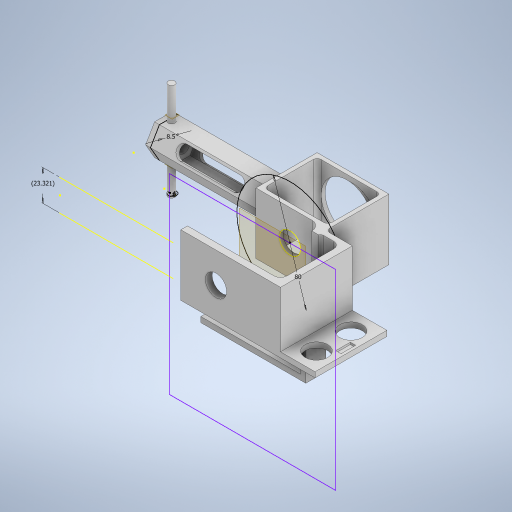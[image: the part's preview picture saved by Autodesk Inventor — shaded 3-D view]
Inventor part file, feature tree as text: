
AUTODESK INVENTOR PART (.ipt)
format: ipt  version: 2024 (Build 280153000, 153)  size: 843,264 bytes
history: native  units: in
note: dims shown in document units (in); Inventor stores cm internally (conversion verified against a paired STEP export)
features: sketch x53, extrude x47, fillet x12, plane x3
ambient origin geometry x8: Origin, YZ Plane, XZ Plane, XY Plane, X Axis, Y Axis, Z Axis, Center Point
bodies: Solid1 (feature_tree)
feature tree (115):
  extrude  "Extrusion1"  Depth=0.0984in
  extrude  "Extrusion2"  Depth=0.3937in TaperAngle=0.0deg
  extrude  "Extrusion3"  Depth=0.3937in TaperAngle=0.0deg
  extrude  "Extrusion4"  Depth=0.1969in
  fillet  "Fillet1"  Radius=2.7559in
  fillet  "Fillet2"  Radius=0.1969in
  extrude  "Extrusion5"  Depth=0.0984in
  extrude  "Extrusion6"  Depth=1.811in
  extrude  "Extrusion7"  Depth=1.811in TaperAngle=0.0deg
  extrude  "Extrusion8"  Depth=0.1181in
  extrude  "Extrusion9"  Depth=0.1181in TaperAngle=0.0deg
  fillet  "Fillet3"  Radius=0.6693in
  fillet  "Fillet4"  Radius=0.1181in
  plane  "Work Plane1"
  extrude  "Extrusion15"  Depth=0.9843in
  extrude  "Extrusion18"  Depth=0.1181in
  extrude  "Extrusion19"  Depth=0.3937in
  extrude  "Extrusion20"  Depth=0.2756in
  extrude  "Extrusion21"  Depth=0.1969in TaperAngle=0.0deg
  extrude  "Extrusion26"  Depth=0.1575in
  fillet  "Fillet9"  Radius=0.7874in
  fillet  "Fillet10"  Radius=0.1969in
  fillet  "Fillet11"  Radius=1.9685in
  fillet  "Fillet12"  Radius=0.1969in
  fillet  "Fillet13"  Radius=2.7559in
  fillet  "Fillet15"  Radius=11.811in
  plane  "Work Plane2"
  extrude  "Extrusion27"  Depth=0.1181in
  plane  "Work Plane3"
  extrude  "Extrusion28"  Depth=0.1969in
  extrude  "Extrusion29"  Depth=0.1575in
  extrude  "Extrusion30"  Depth=0.315in
  sketch  "Sketch35"  dims[d121=0.1181in d122=0.0in d123=-0.748in]
  extrude  "Extrusion31"  [1 undecoded]
  extrude  "Extrusion32"  Depth=0.1575in
  extrude  "Extrusion33"  Depth=0.7087in
  extrude  "Extrusion34"  Depth=0.1575in
  extrude  "Extrusion35"  Depth=0.1575in
  extrude  "Extrusion36"  Depth=0.2362in TaperAngle=0.0deg
  extrude  "Extrusion37"  Depth=0.1181in TaperAngle=0.0deg
  extrude  "Extrusion38"  Depth=0.4724in
  extrude  "Extrusion39"  Depth=3.1102in TaperAngle=0.0deg
  extrude  "Extrusion40"  Depth=3.937in TaperAngle=0.0deg
  sketch  "Sketch46"  dims[d152=3.1496in d153=0.0in d154=0.4331in]
  extrude  "Extrusion41"  Depth=0.1181in
  extrude  "Extrusion42"  Depth=0.4331in
  extrude  "Extrusion43"  Depth=0.3937in
  extrude  "Extrusion44"  Depth=0.2362in
  extrude  "Extrusion45"  Depth=0.9843in TaperAngle=0.0deg
  extrude  "Extrusion46"  Depth=0.1969in
  extrude  "Extrusion47"  Depth=0.1181in
  fillet  "Fillet16"  Radius=0.1181in
  fillet  "Fillet17"  Radius=0.1181in
  extrude  "Extrusion48"  Depth=0.1181in TaperAngle=0.0deg
  extrude  "Extrusion49"  Depth=0.1969in TaperAngle=0.0deg
  sketch  "Sketch56"  dims[d182=0.6299in d183=39.3701in d184=0.0in]
  extrude  "Extrusion50"  Depth=0.4331in TaperAngle=0.0deg
  extrude  "Extrusion51"  Depth=39.3701in TaperAngle=0.0deg
  extrude  "Extrusion52"  Depth=0.1181in TaperAngle=0.0deg
  extrude  "Extrusion53"  Depth=0.2756in
  sketch  "Sketch61"  dims[d196=1.0236in d197=0.0in d198=0.5118in]
  extrude  "Extrusion54"  Depth=0.1181in TaperAngle=0.0deg
  extrude  "Extrusion55"  Depth=0.1575in
  sketch  "Sketch65"  dims[d204=0.0591in d205=0.0in]
  extrude  "Extrusion57"  Depth=0.5118in
  extrude  "Extrusion58"  Depth=1.0236in TaperAngle=0.0deg
  extrude  "Extrusion59"  Depth=0.4331in
  sketch  "Sketch69"  dims[d209=1.063in d210=0.0in]
  sketch  "Sketch72"  dims[d211=3.1496in d212=0.1575in d213=2.9528in d214=0.0in d215=0.1575in d216=0.0in d221=0.5906in d222=0.7874in d223=0.0in d224=0.1969in d225=0.1969in d226=3.937in d227=0.0in d228=0.3937in d229=0.5906in d230=0.0in d231=0.8661in d232=0.1378in d233=0.0in d234=0.3346in d37=0.0in d38=0.0in d39=0.0in d74=0.0197in d75=0.0344in d238=0.0197in d239=0.0344in d240=0.0197in d241=0.0344in d242=0.0197in d243=0.0344in]
  sketch  "Sketch1"  dims[d0=0.3937in d1=0.0984in]
  sketch  "Sketch2"  dims[d2=0.3937in d3=0.0in d4=0.0787in d5=0.0in]
  sketch  "Sketch3"  dims[d6=0.3937in d7=0.0787in d8=0.0in]
  sketch  "Sketch4"  dims[d9=0.2362in d10=0.1969in d11=2.7559in d12=0.0in d13=0.1969in]
  sketch  "Sketch5"  dims[d14=0.1575in d15=0.0984in]
  sketch  "Sketch6"  dims[d16=3.1496in d17=0.0in d18=1.811in]
  sketch  "Sketch8"  dims[d19=1.811in d20=2.126in d21=0.0in]
  sketch  "Sketch9"  dims[d22=0.1181in d23=0.1181in]
  sketch  "Sketch10"  dims[d24=0.1181in d25=1.7717in d26=0.0in d27=0.6693in d28=0.1181in d29=0.0in]
  sketch  "Sketch19"  dims[d30=0.9843in d31=0.6299in]
  sketch  "Sketch22"  dims[d32=1.378in d33=0.0in d34=0.1181in]
  sketch  "Sketch23"  dims[d35=0.0787in d36=0.3937in]
  sketch  "Sketch24"  dims[d72=0.3937in d73=0.0in d80=0.2756in]
  sketch  "Sketch25"  dims[d81=1.378in d82=0.1969in d83=0.0in]
  sketch  "Sketch30"  dims[d84=0.1378in d85=0.1575in d86=0.7874in d87=0.0in d88=0.1969in d89=1.9685in d90=0.0in d91=0.1969in d92=2.7559in d93=0.0in d110=11.811in d111=0.0in]
  sketch  "Sketch31"  dims[d112=0.1181in d113=0.1181in]
  sketch  "Sketch32"  dims[d114=0.2677in d115=0.1969in]
  sketch  "Sketch33"  dims[d116=0.1969in d118=0.1575in]
  sketch  "Sketch34"  dims[d119=-0.748in d120=0.315in]
  sketch  "Sketch36"  dims[d124=0.1181in d125=0.0in d126=0.1575in]
  sketch  "Sketch37"  dims[d127=3.937in d128=0.0in d129=0.7087in]
  sketch  "Sketch38"  dims[d130=0.1181in d131=0.0in d132=0.1575in]
  sketch  "Sketch39"  dims[d133=0.2362in d134=0.1575in]
  sketch  "Sketch40"  dims[d135=0.2362in d136=0.6299in d137=0.0in]
  sketch  "Sketch41"  dims[d138=0.7087in d139=0.1181in d140=0.0in]
  sketch  "Sketch42"  dims[d141=3.5827in d142=0.4724in]
  sketch  "Sketch43"  dims[d143=3.1102in d144=3.937in d145=0.0in]
  sketch  "Sketch44"  dims[d146=3.937in d147=0.0in d148=3.937in d149=0.0in]
  sketch  "Sketch45"  dims[d150=0.3937in d151=0.1181in]
  sketch  "Sketch47"  dims[d155=0.0984in d156=0.0in d157=0.3937in]
  sketch  "Sketch49"  dims[d158=0.3937in d159=0.0in d160=0.2362in]
  sketch  "Sketch50"  dims[d161=0.1969in d162=0.9843in d163=0.0in]
  sketch  "Sketch51"  dims[d164=0.2362in d165=0.1969in]
  sketch  "Sketch52"  dims[d166=0.9843in d167=0.0in d168=1.5354in d169=0.1181in d170=0.1181in]
  sketch  "Sketch53"  dims[d171=2.126in d172=0.0in d173=0.1181in d174=0.0in]
  sketch  "Sketch54"  dims[d175=0.1181in d176=0.0in d177=0.1969in d178=0.0in]
  sketch  "Sketch55"  dims[d179=0.1969in d180=0.4331in d181=0.0in]
  sketch  "Sketch57"  dims[d185=1.5354in d186=0.1181in d187=0.0in]
  sketch  "Sketch58"  dims[d188=0.1181in d189=0.2756in]
  sketch  "Sketch59"  dims[d190=0.1969in d191=0.0in d192=0.1181in d193=0.0in]
  sketch  "Sketch60"  dims[d194=0.9181in d195=0.1575in]
  sketch  "Sketch62"  dims[d199=0.6693in d200=1.0236in d201=0.0in]
  sketch  "Sketch63"  dims[d202=0.1575in d203=0.4331in]
  sketch  "Sketch66"  dims[d206=0.0787in]
  sketch  "Sketch67"  dims[d207=0.1575in]
  sketch  "Sketch68"  dims[d208=0.5906in]
note: 1 required parameter value undecoded (feature->parameter linkage not recoverable at this tier; creation-order binding heuristic only, values carry confidence <= 0.55)
